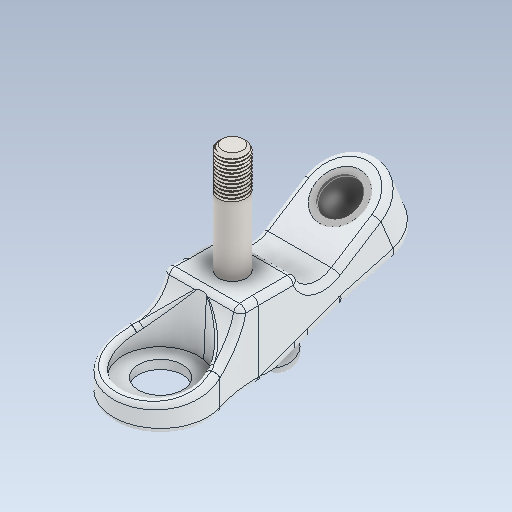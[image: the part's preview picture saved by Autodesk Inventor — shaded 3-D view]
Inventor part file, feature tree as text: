
AUTODESK INVENTOR PART (.ipt)
format: ipt  version: 2021 (Build 250183000, 183)  size: 921,600 bytes
history: mixed  units: in
note: dims shown in document units (in); Inventor stores cm internally (conversion verified against a paired STEP export)
features: fillet x1, revolve x1, thread x1, imported_body x1
ambient origin geometry x8: Origin, YZ Plane, XZ Plane, XY Plane, X Axis, Y Axis, Z Axis, Center Point
bodies: Solid1 (imported_parasolid), Solid2 (imported_parasolid), Solid3 (imported_parasolid)
feature tree (4):
  fillet  "Fillet10"  [1 undecoded]
  revolve  "Revolve2"  [1 undecoded]
  thread  "Thread1"  [1 undecoded]
  imported_body  NMx_Import_Brep_tag  [imported B-rep: ~13 faces, bbox_mm=None]
note: 3 required parameter values undecoded (feature->parameter linkage not recoverable at this tier; creation-order binding heuristic only, values carry confidence <= 0.55)
